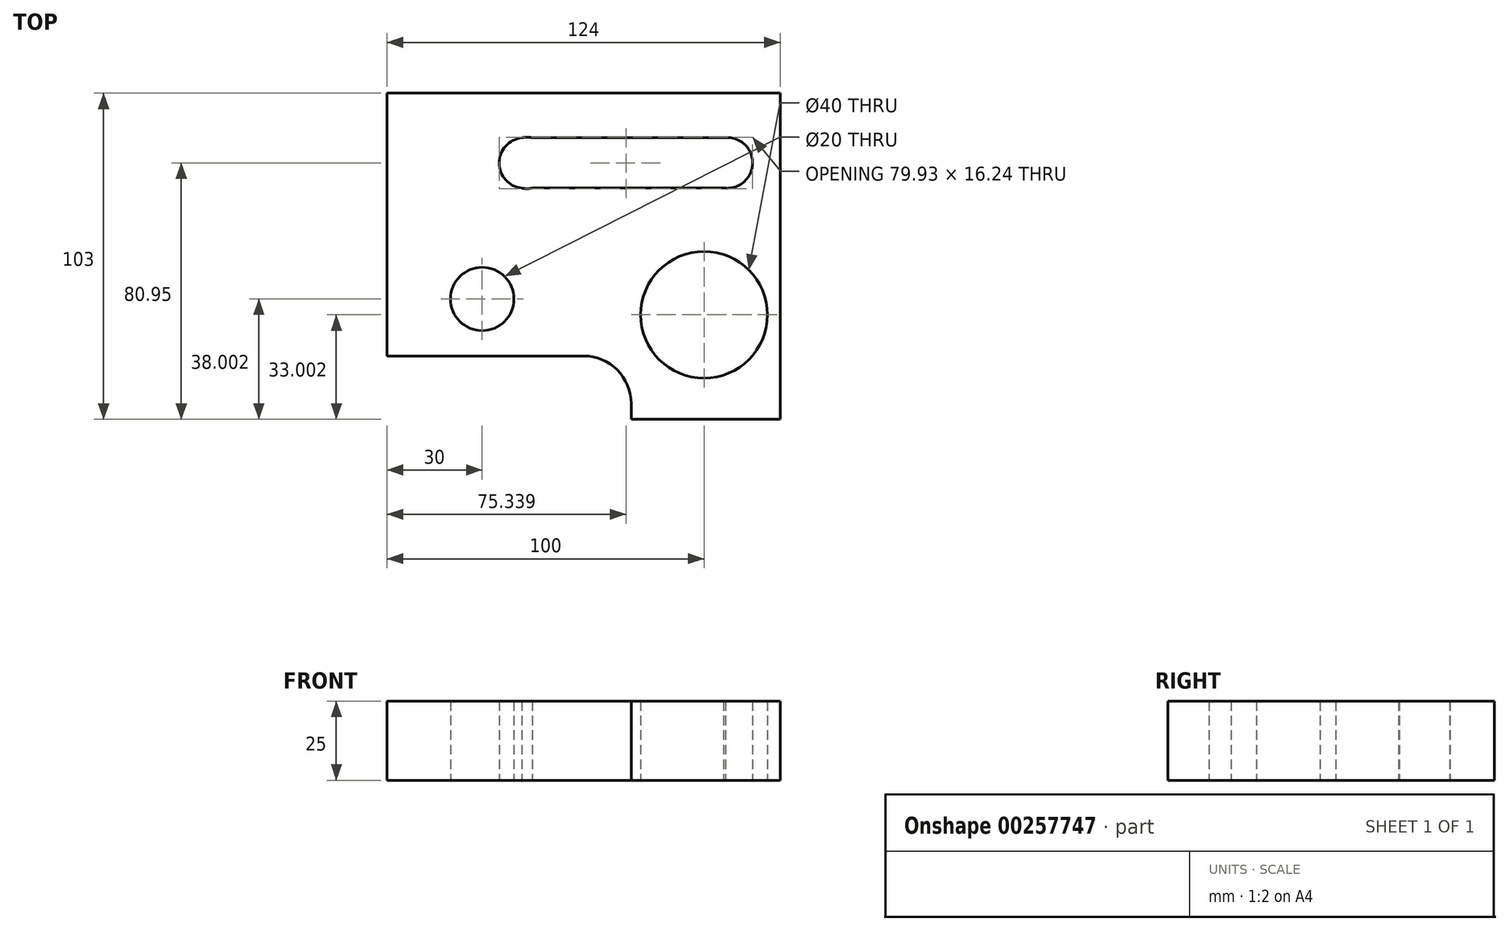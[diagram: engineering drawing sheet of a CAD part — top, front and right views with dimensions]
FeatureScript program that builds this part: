
annotation { "Feature Type Name" : "Feature", "Feature Type Description" : "" }
export const myFeature = defineFeature(function(context is Context, id is Id, definition is map)
    precondition{}
    {
        {
            var Q0;
            Q0=qCreatedBy(makeId("Top.planeOp"),FACE);
            var sketch = newSketch(context, id + "F0", { "sketchPlane" : qUnion([Q0])});
            skLineSegment(sketch, "E0", {"start": v(-56.2, 40.06) * mm, "end": v(-56.2, -42.94) * mm});
            skLineSegment(sketch, "E1", {"start": v(-56.2, -42.94) * mm, "end": v(5.8, -42.94) * mm});
            skLineSegment(sketch, "E2", {"start": v(-56.2, 40.06) * mm, "end": v(67.8, 40.06) * mm});
            skLineSegment(sketch, "E3", {"start": v(67.8, 40.06) * mm, "end": v(67.8, -62.94) * mm});
            skLineSegment(sketch, "E4", {"start": v(20.8, -57.94) * mm, "end": v(20.8, -62.94) * mm});
            skLineSegment(sketch, "E5", {"start": v(67.8, -62.94) * mm, "end": v(20.8, -62.94) * mm});
            skPoint(sketch, "E6.visualSharp", {"position": v(20.8, -42.94) * mm});
            skArc(sketch, "E6.filletArc", {"start": v(20.8, -57.94) * mm, "mid": v(16.4, -47.33) * mm, "end": v(5.8, -42.94) * mm});
            skLineSegment(sketch, "E7", {"start": v(67.8, 40.06) * mm, "end": v(67.8, 26.06) * mm});
            skCircle(sketch, "E8", {"center": v(43.8, -29.94) * mm, "radius": 20 * mm});
            skLineSegment(sketch, "E9", {"start": v(-56.2, -42.94) * mm, "end": v(-26.2, -42.94) * mm});
            skCircle(sketch, "E10", {"center": v(-26.2, -24.94) * mm, "radius": 10 * mm});
            skLineSegment(sketch, "E11", {"start": v(52.3, 25.96) * mm, "end": v(-13.75, 25.96) * mm});
            skLineSegment(sketch, "E12", {"start": v(-13.74, 10.06) * mm, "end": v(51.62, 10.06) * mm});
            skArc(sketch, "E13", {"start": v(-10.41, 25.96) * mm, "mid": v(-12.08, 26.13) * mm, "end": v(-13.75, 25.96) * mm});
            skArc(sketch, "E14", {"start": v(50.6, 10.06) * mm, "mid": v(59.1, 18.39) * mm, "end": v(49.92, 25.96) * mm});
            skPoint(sketch, "E15.orphan", {"position": v(59.9, 10.06) * mm});
            skPoint(sketch, "E16.orphan", {"position": v(59.9, 25.96) * mm});
            skArc(sketch, "E17.trimOffspring", {"start": v(-13.74, 10.06) * mm, "mid": v(-12.08, 9.89) * mm, "end": v(-10.42, 10.06) * mm});
            skArc(sketch, "E18", {"start": v(-13.75, 25.96) * mm, "mid": v(-20.83, 18) * mm, "end": v(-13.74, 10.06) * mm});
            skSolve(sketch);
        }
        {
            var Q0;
            Q0=makeQuery(id+"F0.imprint","IMPRINT",FACE,{"disambiguationData":[TD([[makeQuery(id+"F0.imprint","IMPRINT",EDGE,{"derivedFrom":sQuery(id+"F0.wireOp",EDGE,"E0")}),1.0]])]});
            extrude(context, id + "F1", {"entities" : qUnion([Q0]), "depth" : 25 * mm});
        }
    });
